# Revit family: IL-PU04-11 CONJUNTO VALVULA LAVAMANOS PUSH PARED GRICOL
name_source: partatom
category: Plumbing Fixtures
revit_build: Autodesk Revit 2018 (Build: 20170223_1515(x64)
units: mm (PartAtom-declared; Revit-internal decimal feet)

## family parameters
Cut with Voids When Loaded = No
Host = Face
OmniClass Number = 23.31.11.00
Part Type = Normal
Room Calculation Point = No
Round Connector Dimension = Use Diameter
Shared = No

## types (1)
- IL-PU04-11
    Alto = 86 mm  [stored 0.282152 ft]
    Ancho = 150 mm
    Buje = 34.2 mm
    CW Connection = Yes
    Default Elevation = 0 mm  [stored 0 ft]
    Description = Valvula
    Escudo = 86 mm  [stored 0.282152 ft]
    HW Connection = Yes
    Laton = Laton
    Link Ficha Tecnica = http://infotecnica.gricol.com
    Manufacturer = Gricol
    Metal - ABS Cromado = Plastico - ABS Cromado
    Metal - Acero inoxidable = Metal - Acero inoxidable
    Model = IL-PU04-11
    Product Name = CONJUNTO VALVULA LAVAMANOS PUSH PARED GRICOL
    Type Image = <None>
    URL = https://www.gricol.com
    Vent Connection = No
    Waste Connection = No

note: [stored X ft] marks values corroborated as IEEE doubles in the binary element streams (Revit-internal decimal feet)

## geometry (parser evidence)
native form markers: Blend x2, Sweep x4
no freeform markers — native parametric forms only
